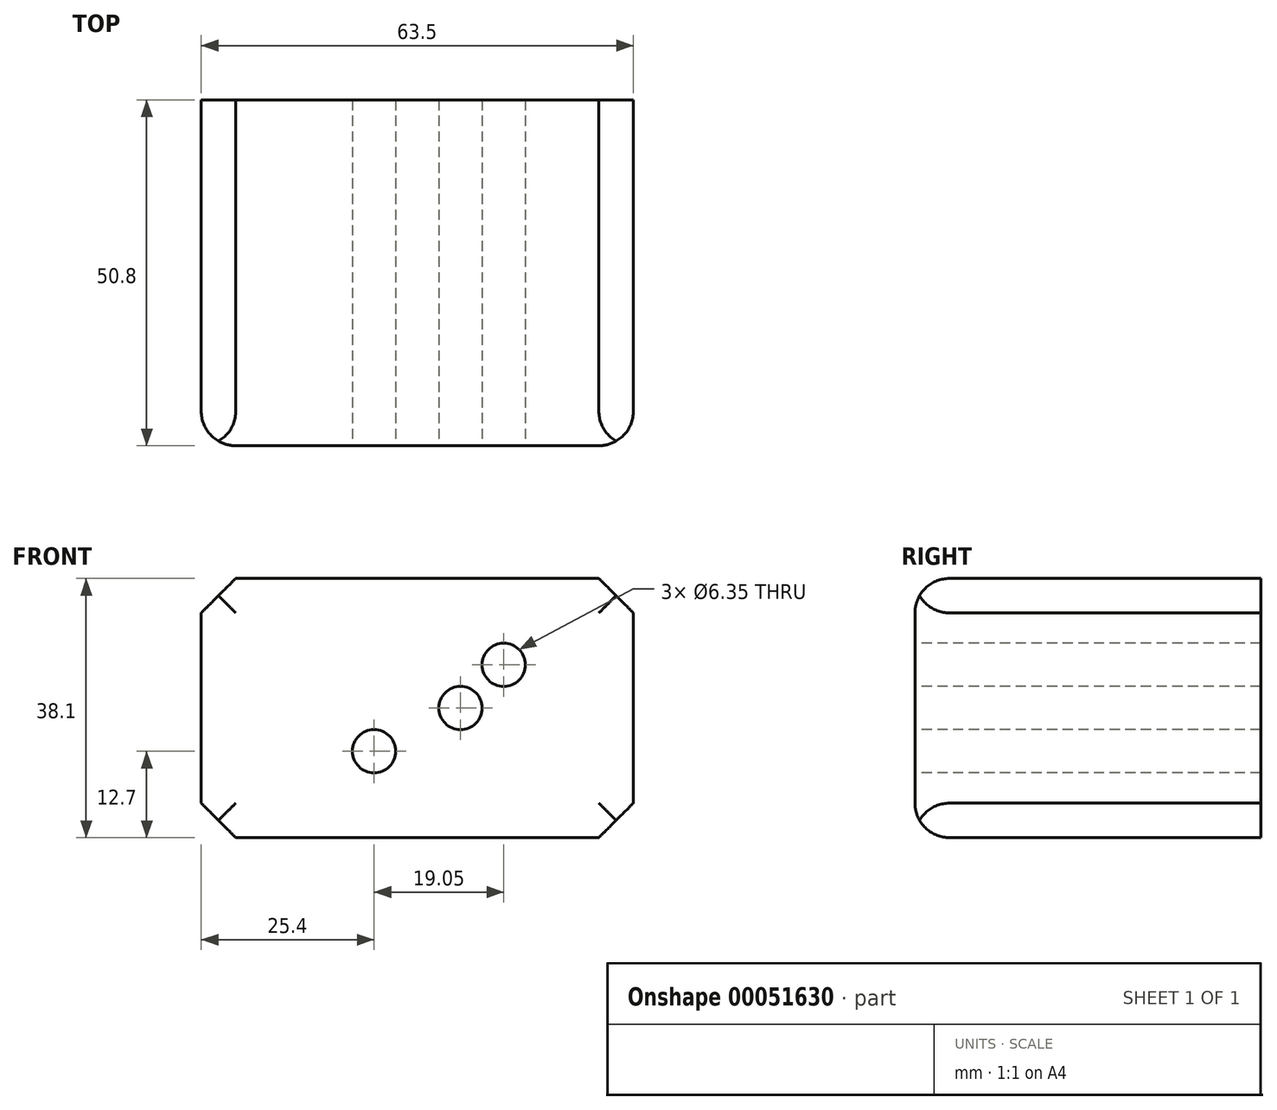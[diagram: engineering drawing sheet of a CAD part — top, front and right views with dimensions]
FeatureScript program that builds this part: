
annotation { "Feature Type Name" : "Feature", "Feature Type Description" : "" }
export const myFeature = defineFeature(function(context is Context, id is Id, definition is map)
    precondition{}
    {
        {
            var Q0;
            Q0=qCreatedBy(makeId("Front.planeOp"),FACE);
            var sketch = newSketch(context, id + "F0", { "sketchPlane" : qUnion([Q0])});
            skLineSegment(sketch, "E0.bottom", {"start": v(0, 0) * mm, "end": v(63.5, 0) * mm});
            skLineSegment(sketch, "E0.top", {"start": v(0, 38.1) * mm, "end": v(63.5, 38.1) * mm});
            skLineSegment(sketch, "E0.left", {"start": v(0, 0) * mm, "end": v(0, 38.1) * mm});
            skLineSegment(sketch, "E0.right", {"start": v(63.5, 0) * mm, "end": v(63.5, 38.1) * mm});
            skSolve(sketch);
        }
        {
            var Q0;
            Q0=makeQuery(id+"F0.imprint","IMPRINT",FACE,{"disambiguationData":[TD([[makeQuery(id+"F0.imprint","IMPRINT",EDGE,{"derivedFrom":sQuery(id+"F0.wireOp",EDGE,"E0.bottom")}),1.0]])]});
            extrude(context, id + "F1", {"entities" : qUnion([Q0]), "oppositeDirection" : true, "depth" : 50.8 * mm});
        }
        {
            var Q0;
            Q0=makeQuery(id+"F1.opExtrude","SWEPT_EDGE",EDGE,{"disambiguationData":[OSD([sQuery(id+"F0.wireOp",EDGE,"E0.top"),sQuery(id+"F0.wireOp",EDGE,"E0.right")])]});
            var Q1;
            Q1=makeQuery(id+"F1.opExtrude","SWEPT_EDGE",EDGE,{"disambiguationData":[OSD([sQuery(id+"F0.wireOp",EDGE,"E0.top"),sQuery(id+"F0.wireOp",EDGE,"E0.left")])]});
            var Q2;
            Q2=makeQuery(id+"F1.opExtrude","SWEPT_EDGE",EDGE,{"disambiguationData":[OSD([sQuery(id+"F0.wireOp",EDGE,"E0.bottom"),sQuery(id+"F0.wireOp",EDGE,"E0.right")])]});
            var Q3;
            Q3=makeQuery(id+"F1.opExtrude","SWEPT_EDGE",EDGE,{"disambiguationData":[OSD([sQuery(id+"F0.wireOp",EDGE,"E0.bottom"),sQuery(id+"F0.wireOp",EDGE,"E0.left")])]});
            chamfer(context, id + "F2", {"entities" : qUnion([Q0, Q1, Q2, Q3]), "width" : 5.08 * mm, "tangentPropagation" : true});
        }
        {
            var Q0;
            Q0=makeQuery(id+"F1.opExtrude","CAP_EDGE",EDGE,{"disambiguationData":[OSD([sQuery(id+"F0.wireOp",EDGE,"E0.right")])],"isStart":true});
            var Q1;
            Q1=makeQuery(id+"F1.opExtrude","CAP_EDGE",EDGE,{"disambiguationData":[OSD([sQuery(id+"F0.wireOp",EDGE,"E0.left")])],"isStart":true});
            var Q2;
            Q2=makeQuery(id+"F1.opExtrude","CAP_EDGE",EDGE,{"disambiguationData":[OSD([sQuery(id+"F0.wireOp",EDGE,"E0.bottom")])],"isStart":true});
            var Q3;
            Q3=makeQuery(id+"F1.opExtrude","CAP_EDGE",EDGE,{"disambiguationData":[OSD([sQuery(id+"F0.wireOp",EDGE,"E0.top")])],"isStart":true});
            fillet(context, id + "F3", {"entities" : qUnion([Q0, Q1, Q2, Q3]), "radius" : 5.08 * mm, "tangentPropagation" : true, "allowEdgeOverflow" : false});
        }
        {
            var Q0;
            Q0=makeQuery(id+"F1.opExtrude","CAP_FACE",FACE,{"disambiguationData":[OSD([sQuery(id+"F0.wireOp",EDGE,"E0.bottom"),sQuery(id+"F0.wireOp",EDGE,"E0.top"),sQuery(id+"F0.wireOp",EDGE,"E0.left"),sQuery(id+"F0.wireOp",EDGE,"E0.right")])],"isStart":true});
            var sketch = newSketch(context, id + "F4", { "sketchPlane" : qUnion([Q0])});
            skPoint(sketch, "E1", {"position": v(25.4, 12.7) * mm});
            skPoint(sketch, "E2", {"position": v(38.1, 19.05) * mm});
            skPoint(sketch, "E3", {"position": v(44.45, 25.4) * mm});
            skSolve(sketch);
        }
        {
            var Q0;
            Q0=sQuery(id+"F4.wireOp",VERTEX,"E1");
            var Q1;
            Q1=sQuery(id+"F4.wireOp",VERTEX,"E3");
            var Q2;
            Q2=sQuery(id+"F4.wireOp",VERTEX,"E2");
            var Q3;
            Q3=makeQuery(id+"F1.opExtrude","SWEPT_BODY",BODY,{"disambiguationData":[OSD([sQuery(id+"F0.wireOp",EDGE,"E0.bottom"),sQuery(id+"F0.wireOp",EDGE,"E0.top"),sQuery(id+"F0.wireOp",EDGE,"E0.left"),sQuery(id+"F0.wireOp",EDGE,"E0.right")])]});
            hole(context, id + "F5", {"style" : HoleStyle.SIMPLE, "holeDiameter" : 6.35 * mm, "endStyle" : HoleEndStyle.THROUGH, "locations" : qUnion([Q0, Q1, Q2]), "scope" : qUnion([Q3])});
        }
    });
